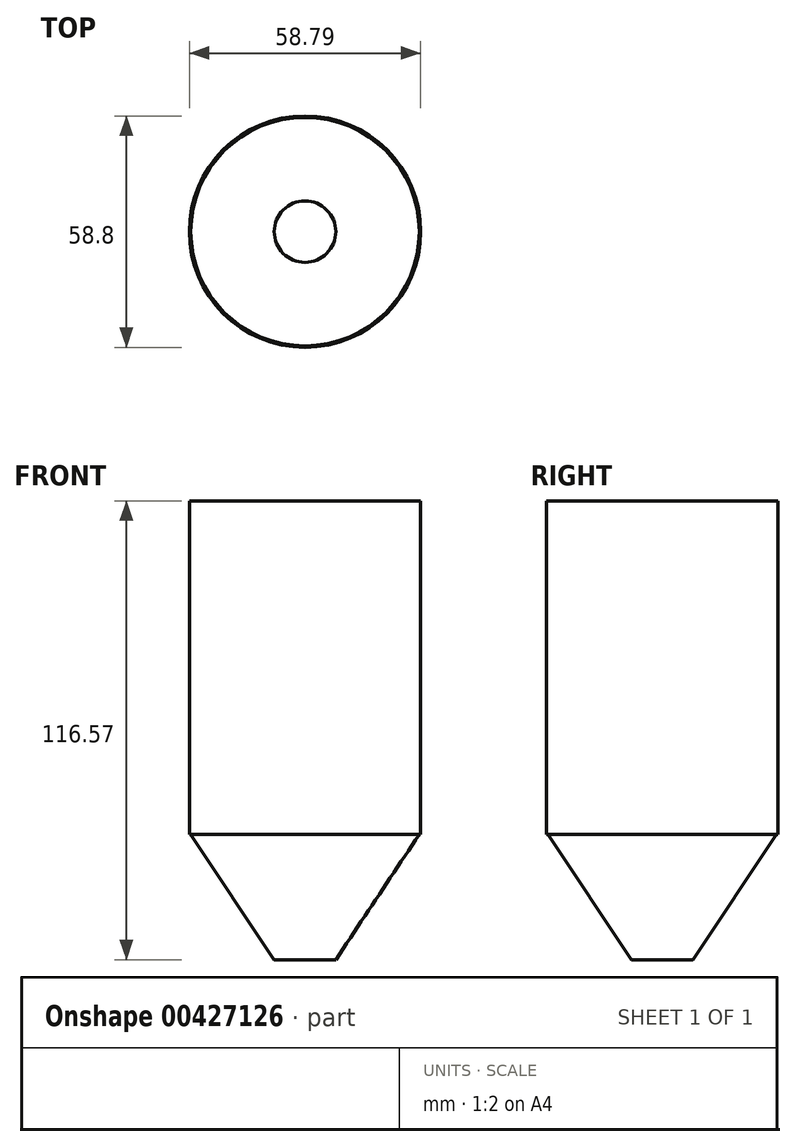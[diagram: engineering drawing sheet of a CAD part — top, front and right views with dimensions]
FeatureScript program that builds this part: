
annotation { "Feature Type Name" : "Feature", "Feature Type Description" : "" }
export const myFeature = defineFeature(function(context is Context, id is Id, definition is map)
    precondition{}
    {
        {
            var Q0;
            Q0=qCreatedBy(makeId("Front.planeOp"),FACE);
            var sketch = newSketch(context, id + "F0", { "sketchPlane" : qUnion([Q0])});
            skLineSegment(sketch, "E0", {"start": v(-53.32, 62.56) * mm, "end": v(-53.32, -22.18) * mm});
            skLineSegment(sketch, "E1", {"start": v(-52.95, -22.18) * mm, "end": v(-31.74, -54.01) * mm});
            skLineSegment(sketch, "E2", {"start": v(-23.92, -53.25) * mm, "end": v(-23.92, 69.71) * mm});
            skSolve(sketch);
        }
        {
            var Q0;
            Q0=sQuery(id+"F0.wireOp",EDGE,"E0");
            var Q1;
            Q1=sQuery(id+"F0.wireOp",EDGE,"E1");
            var Q2;
            Q2=sQuery(id+"F0.wireOp",EDGE,"E2");
            revolve(context, id + "F1", {"bodyType" : ToolBodyType.SURFACE, "surfaceEntities" : qUnion([Q0, Q1]), "axis" : qUnion([Q2]), "revolveType" : RevolveType.FULL});
        }
    });
